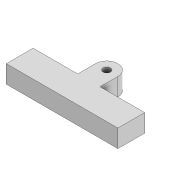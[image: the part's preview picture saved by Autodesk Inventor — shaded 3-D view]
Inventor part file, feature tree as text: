
AUTODESK INVENTOR PART (.ipt)
format: ipt  version: 2022 (Build 260153000, 153)  size: 93,184 bytes
history: native  units: mm
features: extrude x1, sketch x1
ambient origin geometry x8: Origin, YZ Plane, XZ Plane, XY Plane, X Axis, Y Axis, Z Axis, Center Point
bodies: Solid1 (feature_tree)
feature tree (2):
  extrude  "Extrusion1"  Depth=10.0mm
  sketch  "Sketch1"  dims[d0=3.3mm d1=10.0mm d2=20.0mm d3=8.0mm d4=0.0mm d5=12.0mm d6=20.0mm d7=20.0mm]
